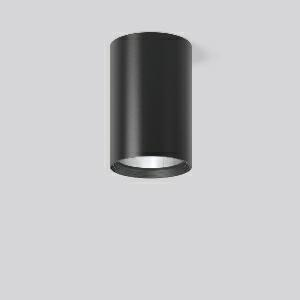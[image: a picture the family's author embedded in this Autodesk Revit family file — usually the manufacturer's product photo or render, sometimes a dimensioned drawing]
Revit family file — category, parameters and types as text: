
# Revit family: heledon_maxi_a_931226_003_3_5e40
name_source: partatom
category: Lighting Fixtures
units: mm (PartAtom-declared; Revit-internal decimal feet)

## family parameters
Cut with Voids When Loaded = No
Host = Face
Light Source = No
Part Type = Normal
Room Calculation Point = No
Round Connector Dimension = Use Diameter
Shared = No

## types (1)
- HELEDON maxi A (1 x LED Modul 935, 4200 lm, 3500)
    Apparent Load = 35 VA
    Approval mark = CE
    CIE Flux Codes = 97 100 100 100 100
    Color Rendering = 92
    Color Temperature = 3500
    Default Elevation = 1800 mm
    Description = Series: HELEDON maxi
Cylindrical surface-mounted downlight. Housing: die-cast aluminium, powder-coated. Internal ceiling frame polycarbonate with bayonet mounting. Black plastic ring and recessed LED to prevent glare from the side. Optical assembly with reflector made of MIRO-Silver with 98% total light reflection for outstanding efficiency - can be changed without tools. Best colour rendering index Ra>90. Suitable for Ceiling mounting. Easy installation with a separate ceiling frame with bayonet mounting and plug connection. Driver integrated. Connected via plug-in connector. High quality converter without flickering and stroboscopic effect. The following accessories can be mounted without use of tools: interchangeable lenses, decorative glasses, honeycomb louvre, clear and frosted diffusers, white interchangeable plastic ring. 
Colour: deep black, matt (RAL 9005)
Diameter: 123 mm
Height: 183 mm
Lamp: LED
Socket: without socket
Colour temperature: 3500K
Colour rendering index (CRI): 92
System power: 35 W
Rated luminous flux: 4200 lm
Luminous efficiency: 120 lm/W
Control gear: Regulated power supply
Protection class: I
Type of protection: IP 20
    Height = 183 mm
    Lamp = 1 x LED Modul 935
    Lamp Light Flux = 4200 lm
    Lamp count = 1
    Length = 123 mm
    Lifetime = 50000 h
    Luminous efficacy = 120 lm/W
    Manufacturer = RZB
    ModVariant = No
    Model = 931226.003.3
    Mounting Place = Ceiling
    Mounting Type = Surface mounted
    Number of Poles = 1
    OnlyDefault = Yes
    Power Factor = 1
    Product Name = HELEDON maxi A
    Product group = Surface mounted downlights
    ProductGroupID = 302
    Protection Class = Protection class I
    Protection Degree = IP 20
    RLX_Detail_Level = 1
    RLX_Emergency_Light_Flux = 0 lm
    RLX_Emergency_Type = 0
    RLX_Emergency_Type_DB = No
    RlxData = <blob elided: 95625 chars, md5=ad30d0f6>
    Socket = socket
    Standby Power = 0 W
    System Light Flux = 4200 lm
    System Power = 35 W
    Type Comments = Product without accessories
    Type Image = 931192.003.jpg
    URL = http://relux.com
    VarID = ---
    Voltage = 230 V
    Voltage Range = 220-240 V
    Weight = 0.00 kg
    Width = 0 mm  [stored 0 ft]

note: [stored X ft] marks values corroborated as IEEE doubles in the binary element streams (Revit-internal decimal feet)

## geometry (parser evidence)
native form markers: Blend x4, Sweep x9
no freeform markers — native parametric forms only
